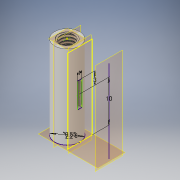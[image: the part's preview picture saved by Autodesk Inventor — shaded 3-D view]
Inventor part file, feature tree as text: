
AUTODESK INVENTOR PART (.ipt)
format: ipt  version: 2019.3 (Build 233278000, 278)  size: 754,688 bytes
history: native  units: in
note: dims shown in document units (in); Inventor stores cm internally (conversion verified against a paired STEP export)
features: sketch x8, other x6, extrude x4, thread x1, revolve x1, projected_geometry x1
ambient origin geometry x8: Origin, YZ Plane, XZ Plane, XY Plane, X Axis, Y Axis, Z Axis, Center Point
bodies: Body1 (feature_tree), Body2 (feature_tree)
feature tree (21):
  other  "ソリッド1"
  sketch  "スケッチ2"
  sketch  "スケッチ1"
  extrude  "押し出し1"  Depth=0.0866in
  extrude  "押し出し2"  Depth=0.0217in
  other  "作業平面1"
  other  "作業平面2"
  sketch  "スケッチ6"
  extrude  "押し出し4"  Depth=0.7874in TaperAngle=0.0deg
  sketch  "スケッチ10"
  other  "作業平面3"
  sketch  "スケッチ11"
  extrude  "押し出し6"  Depth=0.1102in TaperAngle=0.0deg
  thread  "ねじ7"
  revolve  "回転4"
  other  "コイル4"
  projected_geometry  "投影ループ2"
  sketch  "スケッチ16"
  sketch  "スケッチ19"
  sketch  "スケッチ20"
  other  "ソリッド5"
